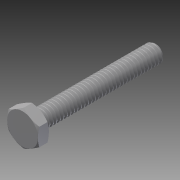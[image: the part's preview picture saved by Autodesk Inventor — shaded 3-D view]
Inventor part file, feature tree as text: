
AUTODESK INVENTOR PART (.ipt)
format: ipt  version: 2014 SP1 (Build 180222100, 222)  size: 876,032 bytes
history: native  units: in
note: dims shown in document units (in); Inventor stores cm internally (conversion verified against a paired STEP export)
features: extrude x1, other x1, imported_body x1
ambient origin geometry x8: Origin, YZ Plane, XZ Plane, XY Plane, X Axis, Y Axis, Z Axis, Center Point
bodies: Body1 (feature_tree)
feature tree (3):
  extrude  "Extrude14"  [1 undecoded]
  other  "92620A5481"
  imported_body  "Base1"
note: 1 required parameter value undecoded (feature->parameter linkage not recoverable at this tier; creation-order binding heuristic only, values carry confidence <= 0.55)
